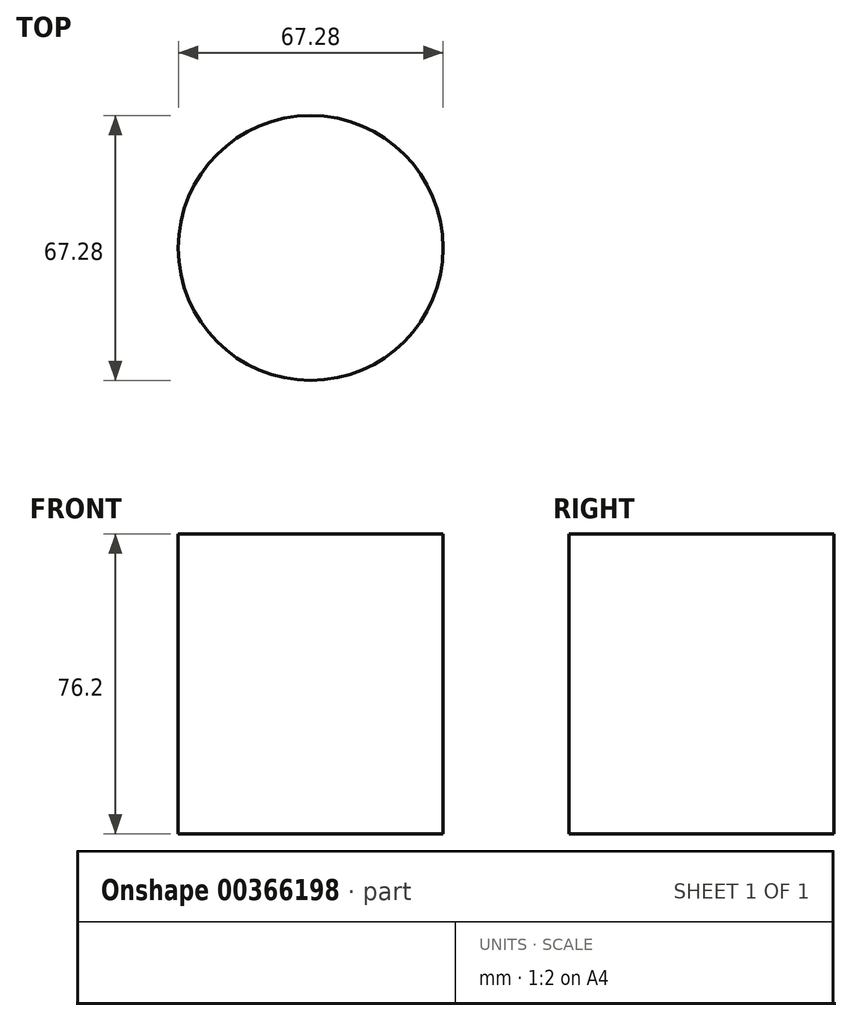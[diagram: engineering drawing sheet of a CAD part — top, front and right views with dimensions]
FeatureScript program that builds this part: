
annotation { "Feature Type Name" : "Feature", "Feature Type Description" : "" }
export const myFeature = defineFeature(function(context is Context, id is Id, definition is map)
    precondition{}
    {
        {
            var Q0;
            Q0=qCreatedBy(makeId("Top.planeOp"),FACE);
            var sketch = newSketch(context, id + "F0", { "sketchPlane" : qUnion([Q0])});
            skCircle(sketch, "E0", {"center": v(0, 0) * mm, "radius": 33.64 * mm});
            skSolve(sketch);
        }
        {
            var Q0;
            Q0 = qSketchRegion(id + "F0", true);
            extrude(context, id + "F1", {"entities" : qUnion([Q0]), "depth" : 76.2 * mm});
        }
        {
            var Q0;
            Q0=makeQuery(id+"F1.opExtrude","CAP_FACE",FACE,{"disambiguationData":[OSD([sQuery(id+"F0.wireOp",EDGE,"E0")])],"isStart":false});
            var sketch = newSketch(context, id + "F2", { "sketchPlane" : qUnion([Q0])});
            skCircle(sketch, "E1", {"center": v(0, 0) * mm, "radius": 31.21 * mm});
            skSolve(sketch);
        }
        {
            var Q0;
            Q0=sQuery(id+"F2.wireOp",EDGE,"E1");
            extrude(context, id + "F3", {"bodyType" : ToolBodyType.SURFACE, "surfaceEntities" : qUnion([Q0]), "oppositeDirection" : true, "depth" : 40.64 * mm});
        }
    });
